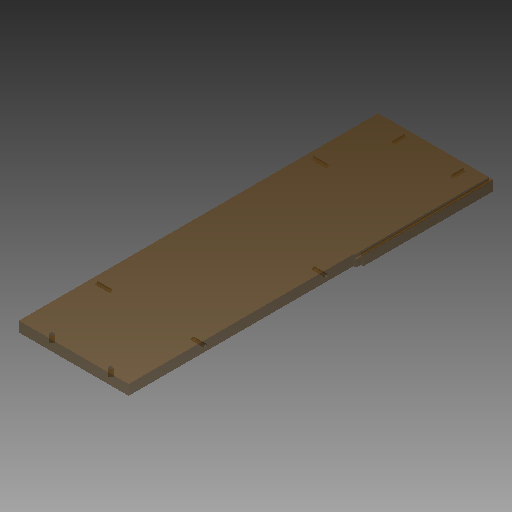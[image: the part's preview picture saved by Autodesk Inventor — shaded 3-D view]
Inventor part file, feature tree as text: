
AUTODESK INVENTOR PART (.ipt)
format: ipt  version: 2018 (Build 220112000, 112)  size: 152,064 bytes
history: native  units: mm
features: extrude x5, hole x4, reference x4, other x4, sketch x2, projected_geometry x1
ambient origin geometry x8: Origin, YZ Plane, XZ Plane, XY Plane, X Axis, Y Axis, Z Axis, Center Point
bodies: Volumenkörper1 (feature_tree)
feature tree (20):
  extrude  "Extrusion1"  Depth=90.0mm
  extrude  "Extrusion2"  Depth=1.2mm
  extrude  "Extrusion3"  Depth=2.5mm
  extrude  "Extrusion4"  Depth=8.0mm TaperAngle=0.0deg
  extrude  "Extrusion5"  Depth=2.0mm
  hole  "Bohrung1"  [1 undecoded]
  hole  "Bohrung2"  [1 undecoded]
  hole  "Bohrung3"  [1 undecoded]
  hole  "Bohrung4"  [1 undecoded]
  sketch  "Skizze6"  dims[d0=281.5mm d1=90.0mm]
  sketch  "Skizze7"  dims[d2=8.0mm d3=0.0mm d4=1.2mm d5=2.5mm d6=8.0mm d7=0.0mm d8=2.0mm d9=4.0mm d10=180.0mm d11=8.0mm d12=0.0mm d13=4.0mm d14=2.0mm d15=5.5mm d16=0.0mm d17=8.0mm d18=0.0mm d19=60.0mm d20=2.459mm d21=10.0mm d22=4.0mm d23=2.0mm d24=90.0deg d25=12.0mm d26=20.594885mm d27=2.459mm d28=8.0mm d29=4.0mm d30=2.0mm d31=90.0deg d32=10.0mm d33=20.594885mm d34=3.2mm d35=8.0mm d36=6.2mm d37=2.0mm d38=90.0deg d39=10.0mm d40=20.594885mm d41=52.0mm d42=4.0mm d43=2.459mm d44=8.0mm d45=6.2mm d46=2.0mm d47=90.0deg d48=10.0mm d49=20.594885mm]
  reference  "Referenz1"
  projected_geometry  "Projizierte Kontur1"
  reference  "Referenz2"
  reference  "Referenz3"
  reference  "Referenz4"
  other  "Käfigaufbau.iam"
  other  "Wand1:1"
  other  "Wand4:1"
  other  "Boden:1"
note: 4 required parameter values undecoded (feature->parameter linkage not recoverable at this tier; creation-order binding heuristic only, values carry confidence <= 0.55)
